# Revit family: Haworth_BuzziBracks_Medium
name_source: partatom
category: Furniture
revit_build: Autodesk Revit 2018 (Build: 20170223_1515(x64)
units: mm (PartAtom-declared; Revit-internal decimal feet)

## family parameters
Always vertical = Yes
Cut with Voids When Loaded = No
OmniClass Number = 23.40.20.00
OmniClass Title = General Furniture and Specialties
Room Calculation Point = No
Shared = No
Work Plane-Based = No

## types (8) — shared parameters
15.5d x 56.75w Shelf = No
15.5d x 88.25w Shelf = No
29.5d x 56.75w Worktop = No
29.5d x 88.25w Worktop = No
Actual Height = 59.5 "
Assembly Code = E2020200
Cable Entry = Yes
Description = Haworth - BuzziBracks - Medium
Full Shelf = No
Full Worktop = No
High Table = No
Large Meeting Table = No
Low Table = Yes
Manufacturer = Haworth
Metal Support 1 Dim. = 14.96 "
Metal Support 2 Dim. = 29.725 "
Metal Support 3 Dim. = 44.49 "
Metal Support 4 Dim. = 58.975 "
Model = HCBZ-BRF
Note = Verify Final Dim. w/ Haworth
Revision = 1
Standard Depths = 47.25 or 59 in.
Standard Widths = 63 or 94.5 in.
URL = http://www.haworth.com
URL - Product = http://www.haworth.com
Warranty = http://www.haworth.com
With Cover = Yes

## per-type parameters (varying)
| type | 47.25d x 63w | 47.25d x 94.5w | 59d x 94.5w | Actual Depth | Actual Width | Asymmetrical | Small Meeting Table | Symmetrical |
| 59d 94.5w - Symmetrical - With Small Meeting Table | No | No | Yes | 59 " | 94.5 " | No | Yes | Yes |
| 59d 94.5w - Asymmetrical - With Small Meeting Table | No | No | Yes | 59 " | 94.5 " | Yes | Yes | No |
| 47.25d 94.5w - Symmetrical - With Small Meeting Table | No | Yes | No | 47.25 " | 94.5 " | No | Yes | Yes |
| 47.25d 94.5w - Asymmetrical - With Small Meeting Table | No | Yes | No | 47.25 " | 94.5 " | Yes | Yes | No |
| 47.25d 63w - Symmetrical - With Small Meeting Table | Yes | No | No | 47.25 " | 63 " | No | Yes | Yes |
| 47.25d 63w - Asymmetrical - With Small Meeting Table | Yes | No | No | 47.25 " | 63 " | Yes | Yes | No |
| 59d 94.5w - Symmetrical - Without Meeting Table | No | No | Yes | 59 " | 94.5 " | No | No | Yes |
| 59d 94.5w - Asymmetrical - Without Meeting Table | No | No | Yes | 59 " | 94.5 " | Yes | No | No |

## geometry (parser evidence)
native form markers: Sweep x19
no freeform markers — native parametric forms only
